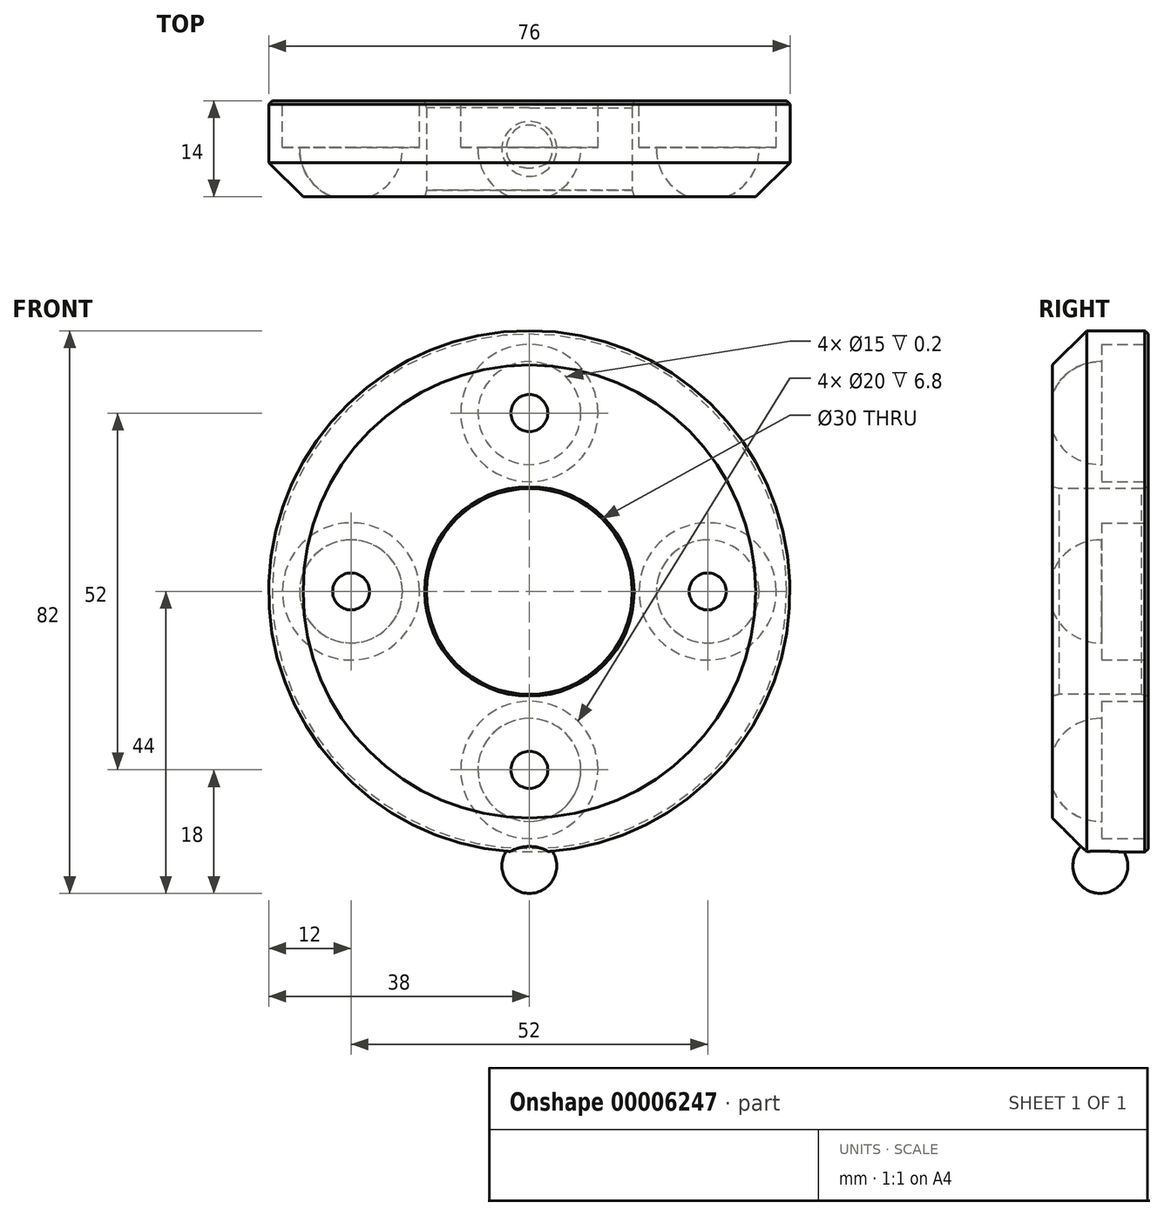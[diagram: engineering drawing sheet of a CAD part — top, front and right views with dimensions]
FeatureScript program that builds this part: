
annotation { "Feature Type Name" : "Feature", "Feature Type Description" : "" }
export const myFeature = defineFeature(function(context is Context, id is Id, definition is map)
    precondition{}
    {
        {
            var Q0;
            Q0=qCreatedBy(makeId("Right.planeOp"),FACE);
            var sketch = newSketch(context, id + "F0", { "sketchPlane" : qUnion([Q0])});
            skLineSegment(sketch, "E0", {"start": v(-36.7, 0) * mm, "end": v(100.7, 0) * mm, "construction": true});
            skLineSegment(sketch, "E1.bottom", {"start": v(0, 15) * mm, "end": v(14, 15) * mm});
            skLineSegment(sketch, "E1.top", {"start": v(0, 38) * mm, "end": v(14, 38) * mm});
            skLineSegment(sketch, "E1.left", {"start": v(0, 15) * mm, "end": v(0, 38) * mm});
            skLineSegment(sketch, "E2", {"start": v(14, 38) * mm, "end": v(14, 15) * mm});
            skSolve(sketch);
        }
        {
            var Q0;
            Q0=makeQuery(id+"F0.imprint","IMPRINT",FACE,{"disambiguationData":[TD([[makeQuery(id+"F0.imprint","IMPRINT",EDGE,{"derivedFrom":sQuery(id+"F0.wireOp",EDGE,"E1.bottom")}),1.0]])]});
            var Q1;
            Q1=sQuery(id+"F0.wireOp",EDGE,"E0");
            revolve(context, id + "F1", {"entities" : qUnion([Q0]), "axis" : qUnion([Q1]), "revolveType" : RevolveType.FULL});
        }
        {
            var Q0;
            Q0=qCreatedBy(makeId("Right.planeOp"),FACE);
            var sketch = newSketch(context, id + "F2", { "sketchPlane" : qUnion([Q0])});
            skLineSegment(sketch, "E3", {"start": v(9, -36.54) * mm, "end": v(9, -33.02) * mm});
            skLineSegment(sketch, "E4", {"start": v(9, -33.02) * mm, "end": v(7, -33.02) * mm});
            skArc(sketch, "E5", {"start": v(7, -44) * mm, "mid": v(10.86, -41.04) * mm, "end": v(9, -36.54) * mm});
            skLineSegment(sketch, "E6", {"start": v(7, -33.02) * mm, "end": v(7, -44) * mm});
            skSolve(sketch);
        }
        {
            var Q0;
            Q0=makeQuery(id+"F2.imprint","IMPRINT",FACE,{"disambiguationData":[TD([[makeQuery(id+"F2.imprint","IMPRINT",EDGE,{"derivedFrom":sQuery(id+"F2.wireOp",EDGE,"E3")}),1.0]])]});
            var Q1;
            Q1=sQuery(id+"F2.wireOp",EDGE,"E6");
            revolve(context, id + "F3", {"operationType" : NewBodyOperationType.ADD, "entities" : qUnion([Q0]), "axis" : qUnion([Q1]), "revolveType" : RevolveType.FULL});
        }
        {
            var Q0;
            Q0=qCreatedBy(makeId("Right.planeOp"),FACE);
            var sketch = newSketch(context, id + "F4", { "sketchPlane" : qUnion([Q0])});
            skPoint(sketch, "E7.center.orphan", {"position": v(14, 26) * mm});
            skLineSegment(sketch, "E8.left", {"start": v(14, 26) * mm, "end": v(14, 25.92) * mm});
            skPoint(sketch, "E9.orphan", {"position": v(0, 26) * mm});
            skArc(sketch, "E10", {"start": v(7, 33.5) * mm, "mid": v(1.7, 31.3) * mm, "end": v(-0.5, 26) * mm});
            skLineSegment(sketch, "E11", {"start": v(-0.5, 26) * mm, "end": v(16.21, 26) * mm});
            skLineSegment(sketch, "E12", {"start": v(16.21, 26) * mm, "end": v(16.21, 33.5) * mm});
            skLineSegment(sketch, "E13", {"start": v(16.21, 33.5) * mm, "end": v(7, 33.5) * mm});
            skSolve(sketch);
        }
        {
            var Q0;
            {var subQ4=sQuery(id+"F4.wireOp",EDGE,"E10");Q0=makeQuery(id+"F4.imprint","IMPRINT",FACE,{"disambiguationData":[TD([[makeQuery(id+"F4.imprint","IMPRINT",EDGE,{"derivedFrom":subQ4}),1.0]])]});}
            var Q1;
            Q1=sQuery(id+"F4.wireOp",EDGE,"E11");
            revolve(context, id + "F5", {"operationType" : NewBodyOperationType.REMOVE, "entities" : qUnion([Q0]), "axis" : qUnion([Q1]), "revolveType" : RevolveType.FULL, "oppositeDirection" : true});
        }
        {
            var Q0;
            Q0=makeQuery(id+"F1.opRevolve","SWEPT_EDGE",EDGE,{"disambiguationData":[OSD([sQuery(id+"F0.wireOp",EDGE,"E1.top"),sQuery(id+"F0.wireOp",EDGE,"E1.left")])]});
            chamfer(context, id + "F6", {"entities" : qUnion([Q0]), "width" : 5 * mm, "tangentPropagation" : true});
        }
        {
            var Q0;
            Q0=makeQuery(id+"F1.opRevolve","SWEPT_EDGE",EDGE,{"disambiguationData":[OSD([sQuery(id+"F0.wireOp",EDGE,"E1.top"),sQuery(id+"F0.wireOp",EDGE,"E2")])]});
            chamfer(context, id + "F7", {"entities" : qUnion([Q0]), "width" : .5 * mm, "tangentPropagation" : true});
        }
        {
            var Q0;
            Q0=makeQuery(id+"F1.opRevolve","SWEPT_EDGE",EDGE,{"disambiguationData":[OSD([sQuery(id+"F0.wireOp",EDGE,"E1.bottom"),sQuery(id+"F0.wireOp",EDGE,"E1.left")])]});
            var Q1;
            Q1=makeQuery(id+"F1.opRevolve","SWEPT_FACE",FACE,{"disambiguationData":[OSD([sQuery(id+"F0.wireOp",EDGE,"E1.bottom")])]});
            chamfer(context, id + "F8", {"entities" : qUnion([Q0, Q1]), "chamferType" : ChamferType.OFFSET_ANGLE, "width" : 1 * mm, "oppositeDirection" : false, "angle" : 15 * degree, "tangentPropagation" : true});
        }
        {
            var Q0;
            Q0=qCreatedBy(makeId("Right.planeOp"),FACE);
            var sketch = newSketch(context, id + "F9", { "sketchPlane" : qUnion([Q0])});
            skLineSegment(sketch, "E14", {"start": v(43.16, 0) * mm, "end": v(-37.16, 0) * mm, "construction": true});
            skSolve(sketch);
        }
        {
            var Q0;
            Q0=makeQuery(id+"F5.boolean.opBoolean","COPY",FACE,{"derivedFrom":makeQuery(id+"F5.opRevolve","SWEPT_FACE",FACE,{"disambiguationData":[OSD([sQuery(id+"F4.wireOp",EDGE,"E13")])]})});
            var Q1;
            Q1=makeQuery(id+"F5.boolean.opBoolean","COPY",FACE,{"derivedFrom":makeQuery(id+"F5.opRevolve","SWEPT_FACE",FACE,{"disambiguationData":[OSD([sQuery(id+"F4.wireOp",EDGE,"E10")])]})});
            var Q2;
            Q2=sQuery(id+"F9.wireOp",EDGE,"E14");
            circularPattern(context, id + "F10", {"faces" : qUnion([Q0, Q1]), "axis" : qUnion([Q2]), "angle" : 360 * degree, "instanceCount" : 4, "equalSpace" : true, "patternType" : PatternType.FACE});
        }
        {
            var Q0;
            Q0=makeQuery(id+"F1.opRevolve","SWEPT_FACE",FACE,{"disambiguationData":[OSD([sQuery(id+"F0.wireOp",EDGE,"E2")])]});
            var sketch = newSketch(context, id + "F11", { "sketchPlane" : qUnion([Q0])});
            skCircle(sketch, "E15", {"center": v(0, 26) * mm, "radius": 10 * mm});
            skCircle(sketch, "E16", {"center": v(-26, 0) * mm, "radius": 10 * mm});
            skCircle(sketch, "E17", {"center": v(26, 0) * mm, "radius": 10 * mm});
            skCircle(sketch, "E18", {"center": v(0, -26) * mm, "radius": 10 * mm});
            skSolve(sketch);
        }
        {
            var Q0;
            Q0 = qSketchRegion(id + "F11", true);
            extrude(context, id + "F12", {"entities" : qUnion([Q0]), "operationType" : NewBodyOperationType.REMOVE, "oppositeDirection" : true, "depth" : 6.8 * mm, "offsetDistance" : 25 * mm});
        }
    });
